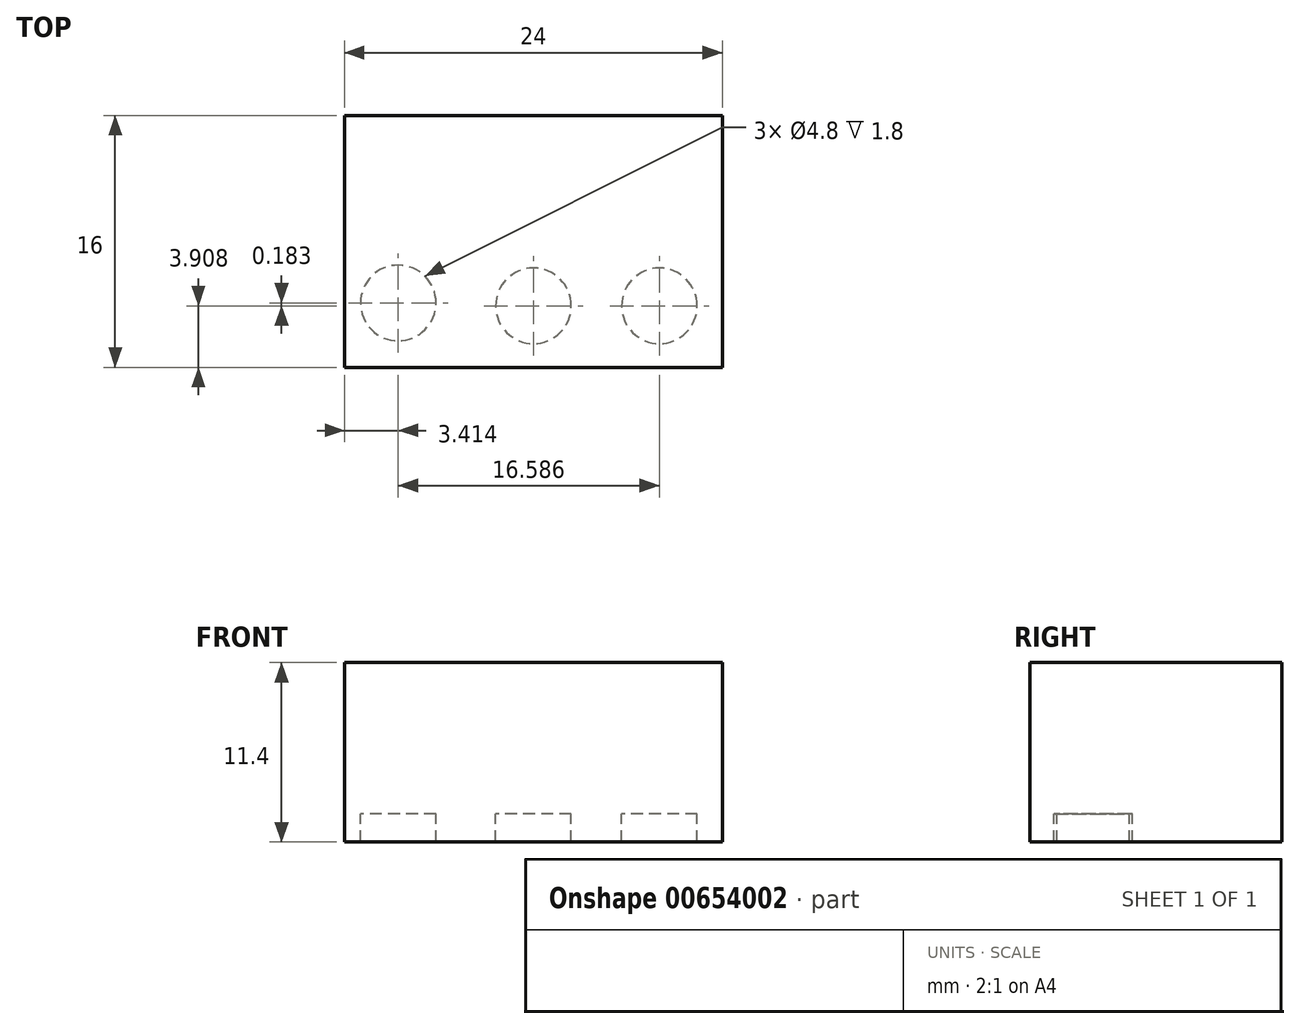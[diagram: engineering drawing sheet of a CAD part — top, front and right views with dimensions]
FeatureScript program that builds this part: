
annotation { "Feature Type Name" : "Feature", "Feature Type Description" : "" }
export const myFeature = defineFeature(function(context is Context, id is Id, definition is map)
    precondition{}
    {
        {
            var Q0;
            Q0=qCreatedBy(makeId("Top.planeOp"),FACE);
            var sketch = newSketch(context, id + "F0", { "sketchPlane" : qUnion([Q0])});
            skLineSegment(sketch, "E0.bottom", {"start": v(0, 0) * mm, "end": v(-24, 0) * mm});
            skLineSegment(sketch, "E0.top", {"start": v(0, 16) * mm, "end": v(-24, 16) * mm});
            skLineSegment(sketch, "E0.left", {"start": v(0, 0) * mm, "end": v(0, 16) * mm});
            skLineSegment(sketch, "E0.right", {"start": v(-24, 0) * mm, "end": v(-24, 16) * mm});
            skSolve(sketch);
        }
        {
            var Q0;
            Q0=makeQuery(id+"F0.imprint","IMPRINT",FACE,{"disambiguationData":[TD([[makeQuery(id+"F0.imprint","IMPRINT",EDGE,{"derivedFrom":sQuery(id+"F0.wireOp",EDGE,"E0.bottom")}),-1.0]])]});
            extrude(context, id + "F1", {"entities" : qUnion([Q0]), "depth" : 9.6 * mm, "offsetDistance" : 25.4 * mm});
        }
        {
            var Q0;
            Q0=qCreatedBy(makeId("Top.planeOp"),FACE);
            var sketch = newSketch(context, id + "F2", { "sketchPlane" : qUnion([Q0])});
            skLineSegment(sketch, "E1", {"start": v(-29.51, 8) * mm, "end": v(0, 8) * mm, "construction": true});
            skLineSegment(sketch, "E2", {"start": v(-16, 19.83) * mm, "end": v(-16, 0) * mm, "construction": true});
            skLineSegment(sketch, "E3", {"start": v(-8, 19.93) * mm, "end": v(-8, 0) * mm, "construction": true});
            skLineSegment(sketch, "E4", {"start": v(-25.17, 15.82) * mm, "end": v(-16, 8) * mm, "construction": true});
            skLineSegment(sketch, "E5", {"start": v(-16, 8) * mm, "end": v(-8, 16.18) * mm, "construction": true});
            skLineSegment(sketch, "E6", {"start": v(-8, 16.18) * mm, "end": v(0, 8) * mm, "construction": true});
            skCircle(sketch, "E7", {"center": v(-20.59, 11.9) * mm, "radius": 2.4 * mm});
            skCircle(sketch, "E8", {"center": v(-12, 12.1) * mm, "radius": 2.4 * mm});
            skCircle(sketch, "E9", {"center": v(-4, 12.1) * mm, "radius": 2.4 * mm});
            skCircle(sketch, "E10.MirrorC", {"center": v(-20.59, 4.1) * mm, "radius": 2.4 * mm});
            skCircle(sketch, "E11.MirrorC", {"center": v(-12, 3.9) * mm, "radius": 2.4 * mm});
            skCircle(sketch, "E12.MirrorC", {"center": v(-4, 3.9) * mm, "radius": 2.4 * mm});
            skLineSegment(sketch, "E13.0.0", {"start": v(0, 0) * mm, "end": v(0, 16) * mm});
            skLineSegment(sketch, "E13.0.1", {"start": v(0, 16) * mm, "end": v(-24, 16) * mm});
            skLineSegment(sketch, "E13.0.2", {"start": v(-24, 16) * mm, "end": v(-24, 0) * mm});
            skLineSegment(sketch, "E13.0.3", {"start": v(-24, 0) * mm, "end": v(0, 0) * mm});
            skSolve(sketch);
        }
        {
            var Q0;
            Q0=makeQuery(id+"F2.imprint","IMPRINT",FACE,{"disambiguationData":[TD([[makeQuery(id+"F2.imprint","IMPRINT",EDGE,{"derivedFrom":sQuery(id+"F2.wireOp",EDGE,"E10.MirrorC")}),-1.0]])]});
            var Q1;
            Q1=makeQuery(id+"F2.imprint","IMPRINT",FACE,{"disambiguationData":[TD([[makeQuery(id+"F2.imprint","IMPRINT",EDGE,{"derivedFrom":sQuery(id+"F2.wireOp",EDGE,"E11.MirrorC")}),-1.0]])]});
            var Q2;
            Q2=makeQuery(id+"F2.imprint","IMPRINT",FACE,{"disambiguationData":[TD([[makeQuery(id+"F2.imprint","IMPRINT",EDGE,{"derivedFrom":sQuery(id+"F2.wireOp",EDGE,"E12.MirrorC")}),-1.0]])]});
            var Q3;
            Q3=makeQuery(id+"F2.imprint","IMPRINT",FACE,{"disambiguationData":[TD([[makeQuery(id+"F2.imprint","IMPRINT",EDGE,{"derivedFrom":sQuery(id+"F2.wireOp",EDGE,"E7")}),1.0]])]});
            var Q4;
            Q4=makeQuery(id+"F2.imprint","IMPRINT",FACE,{"disambiguationData":[TD([[makeQuery(id+"F2.imprint","IMPRINT",EDGE,{"derivedFrom":sQuery(id+"F2.wireOp",EDGE,"E8")}),1.0]])]});
            var Q5;
            Q5=makeQuery(id+"F2.imprint","IMPRINT",FACE,{"disambiguationData":[TD([[makeQuery(id+"F2.imprint","IMPRINT",EDGE,{"derivedFrom":sQuery(id+"F2.wireOp",EDGE,"E9")}),1.0]])]});
            extrude(context, id + "F3", {"entities" : qUnion([Q0, Q1, Q2, Q3, Q4, Q5]), "operationType" : NewBodyOperationType.ADD, "oppositeDirection" : true, "depth" : 1.8 * mm, "offsetDistance" : 25.4 * mm});
        }
    });
